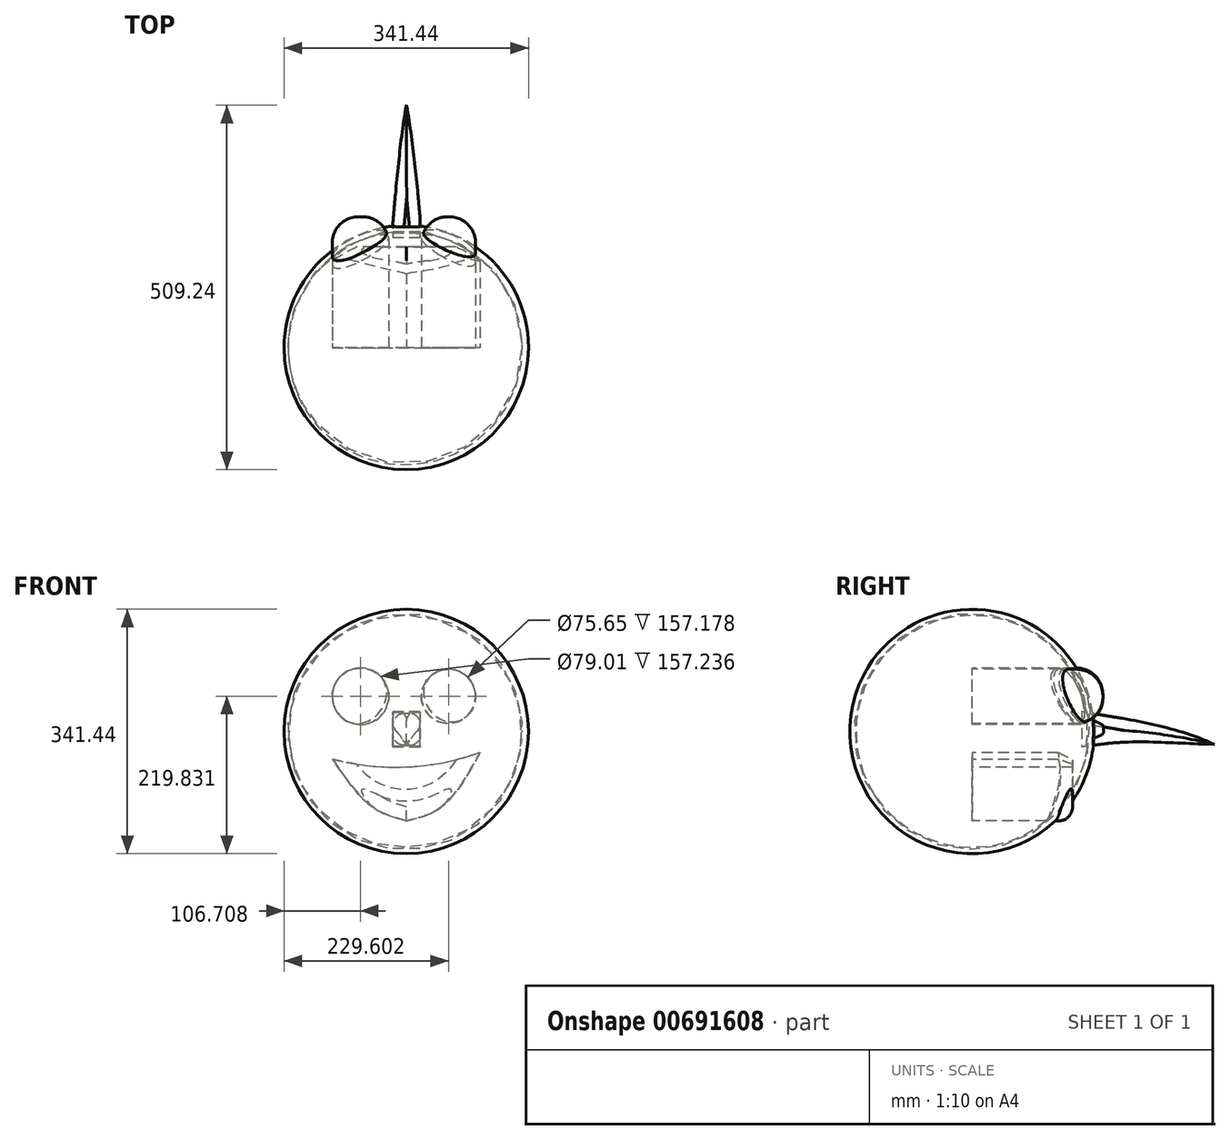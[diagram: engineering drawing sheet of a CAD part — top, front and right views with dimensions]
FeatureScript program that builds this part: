
annotation { "Feature Type Name" : "Feature", "Feature Type Description" : "" }
export const myFeature = defineFeature(function(context is Context, id is Id, definition is map)
    precondition{}
    {
        {
            var Q0;
            Q0=qCreatedBy(makeId("Front.planeOp"),FACE);
            var sketch = newSketch(context, id + "F0", { "sketchPlane" : qUnion([Q0])});
            skCircle(sketch, "E0", {"center": v(0, 0) * mm, "radius": 170.72 * mm});
            skLineSegment(sketch, "E1", {"start": v(-245.6, 0) * mm, "end": v(227.44, 0) * mm, "construction": true});
            skSolve(sketch);
        }
        {
            var Q0;
            Q0=makeQuery(id+"F0.imprint","IMPRINT",FACE,{"disambiguationData":[TD([[makeQuery(id+"F0.imprint","IMPRINT",EDGE,{"derivedFrom":sQuery(id+"F0.wireOp",EDGE,"E0")}),1.0]])]});
            var sketch = newSketch(context, id + "F1", { "sketchPlane" : qUnion([Q0])});
            skLineSegment(sketch, "E2", {"start": v(-217.62, 0) * mm, "end": v(207.45, 0) * mm});
            skSolve(sketch);
        }
        {
            var Q0;
            {var subQ0=sQuery(id+"F1.wireOp",EDGE,"E2");var subQ1=makeQuery(id+"F0.imprint","IMPRINT",EDGE,{"derivedFrom":sQuery(id+"F0.wireOp",EDGE,"E0")});var subQ2=makeQuery(id+"F1.imprint","INTERSECT",VERTEX,{"disambiguationData":[OD(0.0)],"derivedFrom":[subQ1,subQ0]});Q0=makeQuery(id+"F1.imprint","IMPRINT",FACE,{"disambiguationData":[TD([[makeQuery(id+"F1.imprint","IMPRINT",EDGE,{"disambiguationData":[TD([[subQ2,-1.0]])],"derivedFrom":subQ0}),1.0]])]});}
            var Q1;
            Q1=sQuery(id+"F1.wireOp",EDGE,"E2");
            revolve(context, id + "F2", {"entities" : qUnion([Q0]), "axis" : qUnion([Q1]), "revolveType" : RevolveType.FULL});
        }
        {
            var Q0;
            Q0=qCreatedBy(makeId("Front.planeOp"),FACE);
            var sketch = newSketch(context, id + "F3", { "sketchPlane" : qUnion([Q0])});
            skLineSegment(sketch, "E3", {"start": v(-244.63, 0) * mm, "end": v(212.5, 0) * mm, "construction": true});
            skLineSegment(sketch, "E4", {"start": v(-187.37, 0) * mm, "end": v(187.83, 0) * mm});
            skArc(sketch, "E5", {"start": v(161.76, 0) * mm, "mid": v(-1.63, 162.2) * mm, "end": v(-165.03, 0) * mm});
            skSolve(sketch);
        }
        {
            var Q0;
            Q0 = qSketchRegion(id + "F3", true);
            var Q1;
            Q1=sQuery(id+"F3.wireOp",EDGE,"E4");
            revolve(context, id + "F4", {"operationType" : NewBodyOperationType.REMOVE, "entities" : qUnion([Q0]), "axis" : qUnion([Q1]), "revolveType" : RevolveType.FULL, "oppositeDirection" : true});
        }
        {
            var Q0;
            Q0=qCreatedBy(makeId("Right.planeOp"),FACE);
            var sketch = newSketch(context, id + "F5", { "sketchPlane" : qUnion([Q0])});
            skFitSpline(sketch, "E6", {"points": [v(153.24, 27.46) * mm, v(297.74, 0) * mm, v(380.54, -28.78) * mm], "startDerivative": vector(274.67, -43.75) * mm, "endDerivative": vector(175.67, -69.85) * mm});
            skFitSpline(sketch, "E7", {"points": [v(380.54, -28.78) * mm, v(227.45, -14.72) * mm, v(153.24, -21.75) * mm], "startDerivative": vector(-282.95, 35.93) * mm, "endDerivative": vector(-164.57, -25.53) * mm});
            skLineSegment(sketch, "E8", {"start": v(153.24, 27.46) * mm, "end": v(153.24, -21.75) * mm});
            skSolve(sketch);
        }
        {
            var Q0;
            Q0 = qSketchRegion(id + "F5", true);
            extrude(context, id + "F6", {"entities" : qUnion([Q0]), "operationType" : NewBodyOperationType.ADD, "endBound" : BoundingType.SYMMETRIC, "depth" : 38.1 * mm, "offsetDistance" : 25.4 * mm});
        }
        {
            var Q0;
            Q0=qCreatedBy(makeId("Top.planeOp"),FACE);
            var sketch = newSketch(context, id + "F7", { "sketchPlane" : qUnion([Q0])});
            skLineSegment(sketch, "E9", {"start": v(-19.02, 171.68) * mm, "end": v(0, 384.82) * mm});
            skLineSegment(sketch, "E10", {"start": v(0, 384.82) * mm, "end": v(20.21, 171.68) * mm});
            skLineSegment(sketch, "E11", {"start": v(20.21, 171.68) * mm, "end": v(46.72, 222.58) * mm});
            skLineSegment(sketch, "E12", {"start": v(46.72, 222.58) * mm, "end": v(30.82, 444.2) * mm});
            skLineSegment(sketch, "E13", {"start": v(30.82, 444.2) * mm, "end": v(-83.7, 375.28) * mm});
            skLineSegment(sketch, "E14", {"start": v(-83.7, 375.28) * mm, "end": v(-19.02, 171.68) * mm});
            skSolve(sketch);
        }
        {
            var Q0;
            Q0 = qSketchRegion(id + "F7", true);
            extrude(context, id + "F8", {"entities" : qUnion([Q0]), "operationType" : NewBodyOperationType.REMOVE, "endBound" : BoundingType.SYMMETRIC, "depth" : 548.64 * mm, "offsetDistance" : 25.4 * mm});
        }
        {
            var Q0;
            {var subQ2=sQuery(id+"F5.wireOp",EDGE,"E6");Q0=makeQuery(id+"F8.boolean.opBoolean","INTERSECT",EDGE,{"derivedFrom":[makeQuery(id+"F6.boolean.opBoolean","SPLIT",FACE,{"disambiguationData":[TD([makeQuery(id+"F2.opRevolve","SWEPT_FACE",FACE,{"disambiguationData":[OSD([sQuery(id+"F0.wireOp",EDGE,"E0")])]})])],"derivedFrom":makeQuery(id+"F6.opExtrude","SWEPT_FACE",FACE,{"disambiguationData":[OSD([subQ2])]})}),makeQuery(id+"F8.opExtrude","SWEPT_FACE",FACE,{"disambiguationData":[OSD([sQuery(id+"F7.wireOp",EDGE,"E9")])]})]});}
            var Q1;
            {var subQ2=sQuery(id+"F5.wireOp",EDGE,"E7");Q1=makeQuery(id+"F8.boolean.opBoolean","INTERSECT",EDGE,{"derivedFrom":[makeQuery(id+"F6.boolean.opBoolean","SPLIT",FACE,{"disambiguationData":[TD([makeQuery(id+"F2.opRevolve","SWEPT_FACE",FACE,{"disambiguationData":[OSD([sQuery(id+"F0.wireOp",EDGE,"E0")])]})])],"derivedFrom":makeQuery(id+"F6.opExtrude","SWEPT_FACE",FACE,{"disambiguationData":[OSD([subQ2])]})}),makeQuery(id+"F8.opExtrude","SWEPT_FACE",FACE,{"disambiguationData":[OSD([sQuery(id+"F7.wireOp",EDGE,"E9")])]})]});}
            var Q2;
            {var subQ2=sQuery(id+"F5.wireOp",EDGE,"E6");Q2=makeQuery(id+"F8.boolean.opBoolean","INTERSECT",EDGE,{"derivedFrom":[makeQuery(id+"F6.boolean.opBoolean","SPLIT",FACE,{"disambiguationData":[TD([makeQuery(id+"F2.opRevolve","SWEPT_FACE",FACE,{"disambiguationData":[OSD([sQuery(id+"F0.wireOp",EDGE,"E0")])]})])],"derivedFrom":makeQuery(id+"F6.opExtrude","SWEPT_FACE",FACE,{"disambiguationData":[OSD([subQ2])]})}),makeQuery(id+"F8.opExtrude","SWEPT_FACE",FACE,{"disambiguationData":[OSD([sQuery(id+"F7.wireOp",EDGE,"E10")])]})]});}
            var Q3;
            {var subQ2=sQuery(id+"F5.wireOp",EDGE,"E7");Q3=makeQuery(id+"F8.boolean.opBoolean","INTERSECT",EDGE,{"derivedFrom":[makeQuery(id+"F6.boolean.opBoolean","SPLIT",FACE,{"disambiguationData":[TD([makeQuery(id+"F2.opRevolve","SWEPT_FACE",FACE,{"disambiguationData":[OSD([sQuery(id+"F0.wireOp",EDGE,"E0")])]})])],"derivedFrom":makeQuery(id+"F6.opExtrude","SWEPT_FACE",FACE,{"disambiguationData":[OSD([subQ2])]})}),makeQuery(id+"F8.opExtrude","SWEPT_FACE",FACE,{"disambiguationData":[OSD([sQuery(id+"F7.wireOp",EDGE,"E10")])]})]});}
            fillet(context, id + "F9", {"entities" : qUnion([Q0, Q1, Q2, Q3]), "radius" : 16.32 * mm, "tangentPropagation" : true, "allowEdgeOverflow" : false});
        }
        {
            var Q0;
            Q0=qCreatedBy(makeId("Front.planeOp"),FACE);
            var sketch = newSketch(context, id + "F10", { "sketchPlane" : qUnion([Q0])});
            skCircle(sketch, "E15", {"center": v(58.88, 49.11) * mm, "radius": 37.82 * mm});
            skCircle(sketch, "E16", {"center": v(-64.01, 49.11) * mm, "radius": 39.5 * mm});
            skLineSegment(sketch, "E17", {"start": v(135.7, 49.11) * mm, "end": v(-137.56, 49.11) * mm, "construction": true});
            skSolve(sketch);
        }
        {
            var Q0;
            Q0 = qSketchRegion(id + "F10", true);
            extrude(context, id + "F11", {"entities" : qUnion([Q0]), "operationType" : NewBodyOperationType.ADD, "oppositeDirection" : true, "depth" : 182.88 * mm, "offsetDistance" : 25.4 * mm});
        }
        {
            var Q0;
            Q0=makeQuery(id+"F11.opExtrude","CAP_EDGE",EDGE,{"disambiguationData":[OSD([sQuery(id+"F10.wireOp",EDGE,"E15")])],"isStart":false});
            var Q1;
            Q1=makeQuery(id+"F11.opExtrude","CAP_EDGE",EDGE,{"disambiguationData":[OSD([sQuery(id+"F10.wireOp",EDGE,"E16")])],"isStart":false});
            fillet(context, id + "F12", {"entities" : qUnion([Q0, Q1]), "radius" : 36.8 * mm, "tangentPropagation" : true, "allowEdgeOverflow" : false});
        }
        {
            var Q0;
            Q0=qCreatedBy(makeId("Front.planeOp"),FACE);
            var sketch = newSketch(context, id + "F13", { "sketchPlane" : qUnion([Q0])});
            skArc(sketch, "E18", {"start": v(-103.11, -38.87) * mm, "mid": v(0.69, -49.56) * mm, "end": v(103.1, -29.56) * mm});
            skFitSpline(sketch, "E19", {"points": [v(103.1, -29.56) * mm, v(50.5, -104.5) * mm, v(0, -124.99) * mm], "startDerivative": vector(-86.75, -156.97) * mm, "endDerivative": vector(-120.93, -28.36) * mm});
            skFitSpline(sketch, "E20", {"points": [v(0, -124.99) * mm, v(-48.65, -104.5) * mm, v(-103.11, -38.87) * mm], "startDerivative": vector(-113.4, 30.94) * mm, "endDerivative": vector(-93.62, 137.07) * mm});
            skSolve(sketch);
        }
        {
            var Q0;
            Q0 = qSketchRegion(id + "F13", true);
            extrude(context, id + "F14", {"entities" : qUnion([Q0]), "operationType" : NewBodyOperationType.ADD, "oppositeDirection" : true, "depth" : 140.46 * mm, "offsetDistance" : 25.4 * mm});
        }
        {
            var Q0;
            Q0=makeQuery(id+"F14.opExtrude","CAP_EDGE",EDGE,{"disambiguationData":[OSD([sQuery(id+"F13.wireOp",EDGE,"E19")])],"isStart":false});
            var Q1;
            Q1=makeQuery(id+"F14.opExtrude","CAP_EDGE",EDGE,{"disambiguationData":[OSD([sQuery(id+"F13.wireOp",EDGE,"E20")])],"isStart":false});
            fillet(context, id + "F15", {"entities" : qUnion([Q0, Q1]), "radius" : 19 * mm, "tangentPropagation" : true, "allowEdgeOverflow" : false});
        }
    });
